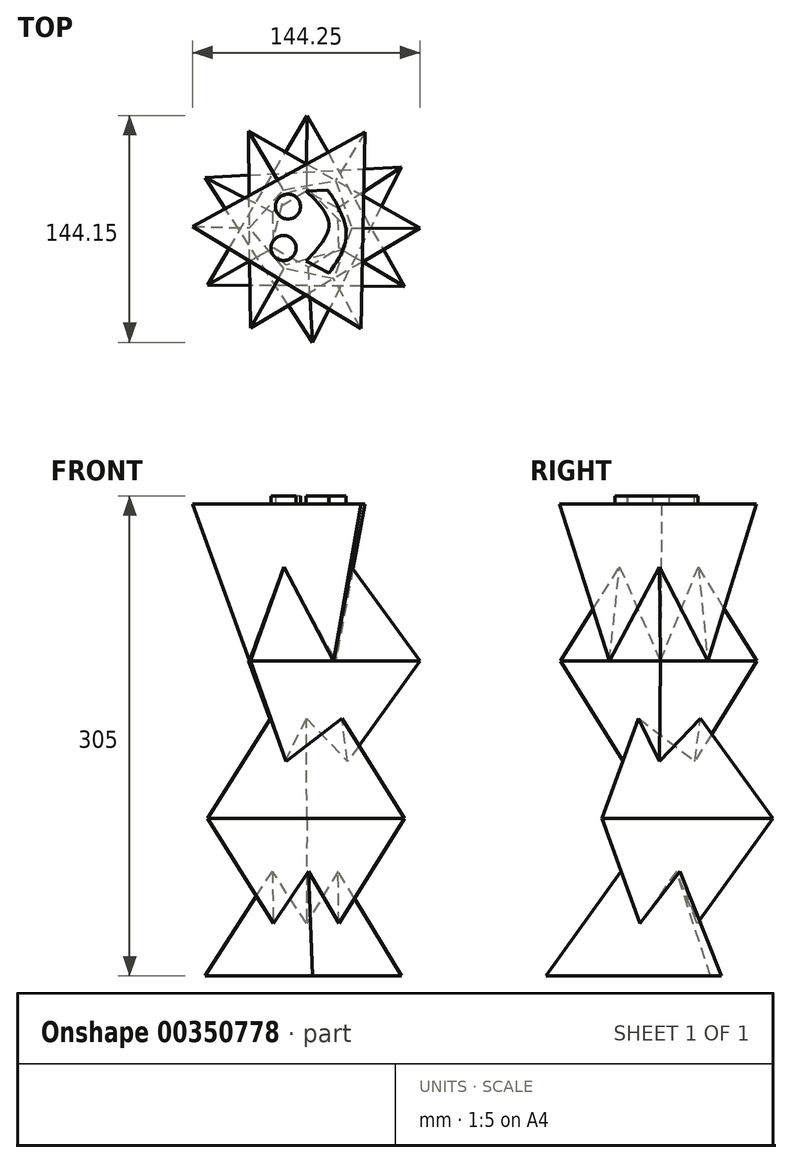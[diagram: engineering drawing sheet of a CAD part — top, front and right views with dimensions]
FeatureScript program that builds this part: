
annotation { "Feature Type Name" : "Feature", "Feature Type Description" : "" }
export const myFeature = defineFeature(function(context is Context, id is Id, definition is map)
    precondition{}
    {
        {
            var Q0;
            Q0=qCreatedBy(makeId("Top.planeOp"),FACE);
            var sketch = newSketch(context, id + "F0", { "sketchPlane" : qUnion([Q0])});
            skCircle(sketch, "E0.cCircle", {"center": v(0, 0) * mm, "radius": 36.07 * mm, "construction": true});
            skLineSegment(sketch, "E0.0", {"start": v(-62.67, -35.71) * mm, "end": v(0.4, 72.13) * mm});
            skLineSegment(sketch, "E0.1", {"start": v(0.4, 72.13) * mm, "end": v(62.26, -36.42) * mm});
            skLineSegment(sketch, "E0.2", {"start": v(62.26, -36.42) * mm, "end": v(-62.67, -35.71) * mm});
            skPoint(sketch, "E0.0.midPoint", {"position": v(-31.13, 18.2) * mm});
            skSolve(sketch);
        }
        {
            var Q0;
            Q0=qCreatedBy(makeId("Top.planeOp"),FACE);
            cPlane(context, id + "F1", {"entities" : qUnion([Q0]), "cplaneType" : CPlaneType.OFFSET, "offset" : 100 * mm, "width" : 152.4 * mm, "height" : 152.4 * mm});
        }
        {
            var Q0;
            Q0=qCreatedBy(id+"F1.planeOp",FACE);
            var sketch = newSketch(context, id + "F2", { "sketchPlane" : qUnion([Q0])});
            skPoint(sketch, "E1", {"position": v(0, 0) * mm});
            skSolve(sketch);
        }
        {
            var Q0;
            Q0=makeQuery(id+"F0.imprint","IMPRINT",FACE,{"disambiguationData":[TD([[makeQuery(id+"F0.imprint","IMPRINT",EDGE,{"derivedFrom":sQuery(id+"F0.wireOp",EDGE,"E0.0")}),-1.0]])]});
            var Q1;
            Q1=sQuery(id+"F2.wireOp",VERTEX,"E1");
            loft(context, id + "F3", {"sheetProfilesArray" : [{ "sheetProfileEntities" : qUnion([Q0]) }, { "sheetProfileEntities" : qUnion([Q1]) }]});
        }
        {
            var Q0;
            Q0=qCreatedBy(id+"F1.planeOp",FACE);
            var sketch = newSketch(context, id + "F4", { "sketchPlane" : qUnion([Q0])});
            skCircle(sketch, "E2.cCircle", {"center": v(0, 0) * mm, "radius": 36.07 * mm, "construction": true});
            skLineSegment(sketch, "E2.0", {"start": v(-36.68, 62.11) * mm, "end": v(72.13, 0.7) * mm});
            skLineSegment(sketch, "E2.1", {"start": v(72.13, 0.7) * mm, "end": v(-35.45, -62.82) * mm});
            skLineSegment(sketch, "E2.2", {"start": v(-35.45, -62.82) * mm, "end": v(-36.68, 62.11) * mm});
            skPoint(sketch, "E2.0.midPoint", {"position": v(17.73, 31.4) * mm});
            skSolve(sketch);
        }
        {
            var Q1;
            Q1=makeQuery(id+"F4.imprint","IMPRINT",FACE,{"disambiguationData":[TD([[makeQuery(id+"F4.imprint","IMPRINT",EDGE,{"derivedFrom":sQuery(id+"F4.wireOp",EDGE,"E2.0")}),-1.0]])]});
            var Q2;
            Q2=qCreatedBy(makeId("Origin.pointOp"),VERTEX);
            loft(context, id + "F5", {"operationType" : NewBodyOperationType.ADD, "sheetProfilesArray" : [{ "sheetProfileEntities" : qUnion([Q1]) }, { "sheetProfileEntities" : qUnion([Q2]) }]});
        }
        {
            var Q0;
            Q0=qCreatedBy(id+"F1.planeOp",FACE);
            cPlane(context, id + "F6", {"entities" : qUnion([Q0]), "cplaneType" : CPlaneType.OFFSET, "offset" : 100 * mm, "width" : 150 * mm, "height" : 150 * mm});
        }
        {
            var Q0;
            Q0=qCreatedBy(id+"F6.planeOp",FACE);
            var sketch = newSketch(context, id + "F7", { "sketchPlane" : qUnion([Q0])});
            skPoint(sketch, "E3", {"position": v(0, 0) * mm});
            skSolve(sketch);
        }
        {
            var Q0;
            Q0=qCreatedBy(makeId("Top.planeOp"),FACE);
            cPlane(context, id + "F8", {"entities" : qUnion([Q0]), "cplaneType" : CPlaneType.OFFSET, "offset" : 100 * mm, "oppositeDirection" : true, "width" : 150 * mm, "height" : 150 * mm});
        }
        {
            var Q0;
            Q0=qCreatedBy(id+"F8.planeOp",FACE);
            var sketch = newSketch(context, id + "F9", { "sketchPlane" : qUnion([Q0])});
            skPoint(sketch, "E4", {"position": v(0, 0) * mm});
            skSolve(sketch);
        }
        {
            var Q1;
            Q1=makeQuery(id+"F5.opLoft","CAP_FACE",FACE,{"disambiguationData":[OSD([makeQuery(id+"F4.imprint","IMPRINT",FACE,{"disambiguationData":[TD([[makeQuery(id+"F4.imprint","IMPRINT",EDGE,{"derivedFrom":sQuery(id+"F4.wireOp",EDGE,"E2.0")}),-1.0]])]})])],"isStart":true});
            var Q2;
            Q2=sQuery(id+"F7.wireOp",VERTEX,"E3");
            loft(context, id + "F10", {"operationType" : NewBodyOperationType.ADD, "sheetProfilesArray" : [{ "sheetProfileEntities" : qUnion([Q1]) }, { "sheetProfileEntities" : qUnion([Q2]) }]});
        }
        {
            var Q1;
            Q1=makeQuery(id+"F3.opLoft","CAP_FACE",FACE,{"disambiguationData":[OSD([makeQuery(id+"F0.imprint","IMPRINT",FACE,{"disambiguationData":[TD([[makeQuery(id+"F0.imprint","IMPRINT",EDGE,{"derivedFrom":sQuery(id+"F0.wireOp",EDGE,"E0.0")}),-1.0]])]})])],"isStart":true});
            var Q2;
            Q2=sQuery(id+"F9.wireOp",VERTEX,"E4");
            loft(context, id + "F11", {"operationType" : NewBodyOperationType.ADD, "sheetProfilesArray" : [{ "sheetProfileEntities" : qUnion([Q1]) }, { "sheetProfileEntities" : qUnion([Q2]) }]});
        }
        {
            var Q0;
            Q0=qCreatedBy(id+"F6.planeOp",FACE);
            var sketch = newSketch(context, id + "F12", { "sketchPlane" : qUnion([Q0])});
            skCircle(sketch, "E5.cCircle", {"center": v(0, 0) * mm, "radius": 36.07 * mm, "construction": true});
            skLineSegment(sketch, "E5.0", {"start": v(34.73, -63.22) * mm, "end": v(-72.12, 1.53) * mm});
            skLineSegment(sketch, "E5.1", {"start": v(-72.12, 1.53) * mm, "end": v(37.39, 61.69) * mm});
            skLineSegment(sketch, "E5.2", {"start": v(37.39, 61.69) * mm, "end": v(34.73, -63.22) * mm});
            skPoint(sketch, "E5.0.midPoint", {"position": v(-18.7, -30.84) * mm});
            skSolve(sketch);
        }
        {
            var Q1;
            Q1=makeQuery(id+"F12.imprint","IMPRINT",FACE,{"disambiguationData":[TD([[makeQuery(id+"F12.imprint","IMPRINT",EDGE,{"derivedFrom":sQuery(id+"F12.wireOp",EDGE,"E5.0")}),-1.0]])]});
            var Q2;
            Q2=qCreatedBy(makeId("Origin.pointOp"),VERTEX);
            loft(context, id + "F13", {"operationType" : NewBodyOperationType.ADD, "sheetProfilesArray" : [{ "sheetProfileEntities" : qUnion([Q1]) }, { "sheetProfileEntities" : qUnion([Q2]) }]});
        }
        {
            var Q0;
            Q0=qCreatedBy(id+"F8.planeOp",FACE);
            var sketch = newSketch(context, id + "F14", { "sketchPlane" : qUnion([Q0])});
            skCircle(sketch, "E6.cCircle", {"center": v(0, 0) * mm, "radius": 36.07 * mm, "construction": true});
            skLineSegment(sketch, "E6.0", {"start": v(60.42, 39.4) * mm, "end": v(3.92, -72.02) * mm});
            skLineSegment(sketch, "E6.1", {"start": v(3.92, -72.02) * mm, "end": v(-64.33, 32.62) * mm});
            skLineSegment(sketch, "E6.2", {"start": v(-64.33, 32.62) * mm, "end": v(60.42, 39.4) * mm});
            skPoint(sketch, "E6.0.midPoint", {"position": v(32.17, -16.31) * mm});
            skSolve(sketch);
        }
        {
            var Q1;
            Q1=makeQuery(id+"F14.imprint","IMPRINT",FACE,{"disambiguationData":[TD([[makeQuery(id+"F14.imprint","IMPRINT",EDGE,{"derivedFrom":sQuery(id+"F14.wireOp",EDGE,"E6.0")}),-1.0]])]});
            var Q2;
            Q2=qCreatedBy(makeId("Origin.pointOp"),VERTEX);
            loft(context, id + "F15", {"operationType" : NewBodyOperationType.ADD, "sheetProfilesArray" : [{ "sheetProfileEntities" : qUnion([Q1]) }, { "sheetProfileEntities" : qUnion([Q2]) }]});
        }
        {
            var Q0;
            Q0=qCreatedBy(id+"F6.planeOp",FACE);
            var sketch = newSketch(context, id + "F16", { "sketchPlane" : qUnion([Q0])});
            skCircle(sketch, "E7", {"center": v(-14.4, -12.1) * mm, "radius": 7.97 * mm});
            skCircle(sketch, "E8", {"center": v(-11.62, 14.2) * mm, "radius": 7.92 * mm});
            skFitSpline(sketch, "E9", {"points": [v(14.45, -28.03) * mm, v(25.12, 0) * mm, v(14, 24.14) * mm, v(13.44, 24.7) * mm], "startDerivative": vector(38.2, 54.69) * mm, "endDerivative": vector(-4.86, 3.52) * mm});
            skFitSpline(sketch, "E10", {"points": [v(0, -20.36) * mm, v(14.45, 3.01) * mm, v(0, 24.14) * mm], "startDerivative": vector(43.1, 46.68) * mm, "endDerivative": vector(-43.62, 42.3) * mm});
            skLineSegment(sketch, "E11", {"start": v(0, -20.36) * mm, "end": v(14.45, -28.03) * mm});
            skLineSegment(sketch, "E12", {"start": v(0, 24.14) * mm, "end": v(13.44, 24.7) * mm});
            skSolve(sketch);
        }
        {
            var Q0;
            Q0=makeQuery(id+"F16.imprint","IMPRINT",FACE,{"disambiguationData":[TD([[makeQuery(id+"F16.imprint","IMPRINT",EDGE,{"derivedFrom":sQuery(id+"F16.wireOp",EDGE,"E7")}),1.0]])]});
            var Q1;
            Q1=makeQuery(id+"F16.imprint","IMPRINT",FACE,{"disambiguationData":[TD([[makeQuery(id+"F16.imprint","IMPRINT",EDGE,{"derivedFrom":sQuery(id+"F16.wireOp",EDGE,"E8")}),1.0]])]});
            var Q2;
            Q2=makeQuery(id+"F16.imprint","IMPRINT",FACE,{"disambiguationData":[TD([[makeQuery(id+"F16.imprint","IMPRINT",EDGE,{"derivedFrom":sQuery(id+"F16.wireOp",EDGE,"E9")}),1.0]])]});
            extrude(context, id + "F17", {"entities" : qUnion([Q0, Q1, Q2]), "operationType" : NewBodyOperationType.ADD, "depth" : 5 * mm});
        }
    });
